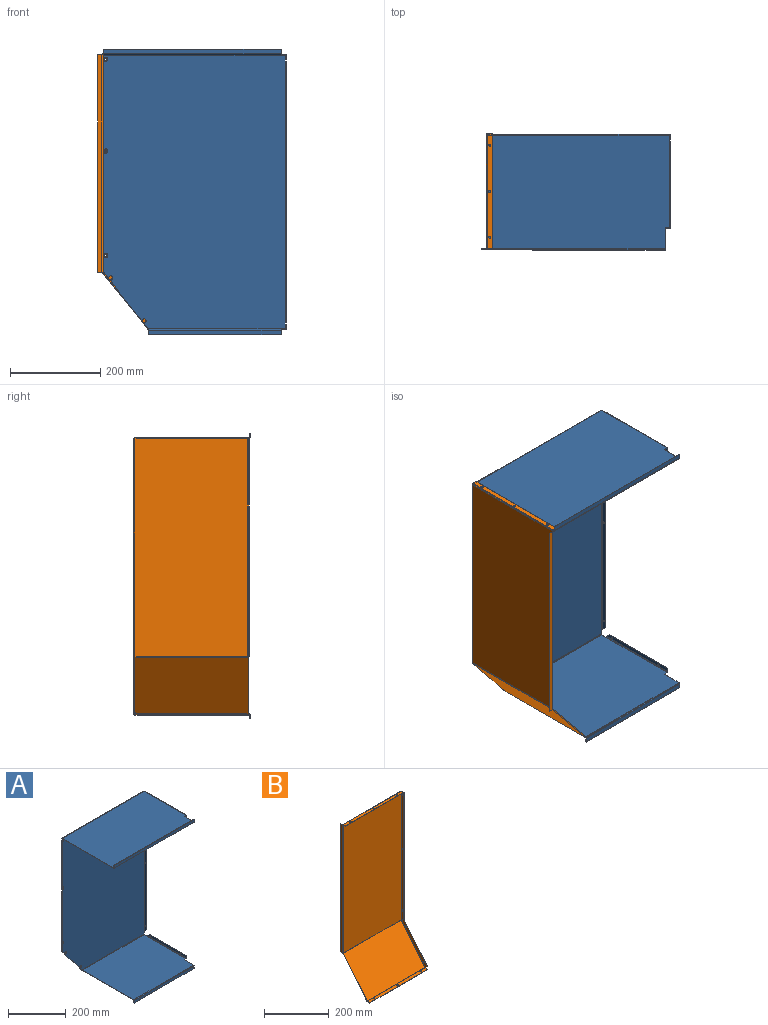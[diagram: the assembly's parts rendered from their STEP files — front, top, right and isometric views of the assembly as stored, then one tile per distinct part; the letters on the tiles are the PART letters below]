
ASSEMBLY  parts=2 mates=1
PART A: 86 faces, bbox 405.1x256.3x634.2 mm
  f0: plane 12.75x1.17mm, normal (1,0,0), area 14.9mm2, adj f14,f15,f25,f50
  f1: plane 7.57x1.17mm, normal (-1,0,0), area 8.8mm2, adj f13,f14,f15,f49
  f2: plane 12.75x1.17mm, normal (1,0,0), area 14.9mm2, adj f14,f15,f24,f29
  f3: plane 13.21x10.19mm, normal (-0.79,0,-0.61), area 19.5mm2, adj f4,f14,f15,f28
  f4: cylinder r=4.76mm len=9.53mm, axis (0,-1,0), area 31.2mm2, adj f3,f5,f14,f15
  f5: plane 92.97x71.75mm, normal (-0.79,0,-0.61), area 137.2mm2, adj f4,f6,f14,f15
  f6: cylinder r=4.76mm len=9.53mm, axis (0,-1,0), area 31.2mm2, adj f5,f7,f14,f15
  f7: plane 15.09x11.65mm, normal (-0.79,0,-0.61), area 22.3mm2, adj f6,f8,f14,f15
  f8: plane 34.52x1.17mm, normal (-1,0,0), area 40.3mm2, adj f7,f9,f14,f15
  f9: cylinder r=4.76mm len=9.53mm, axis (0,-1,0), area 31.2mm2, adj f8,f10,f14,f15
  f10: plane 228.63x1.17mm, normal (-1,0,0), area 267.1mm2, adj f9,f11,f14,f15
  f11: cylinder r=4.76mm len=9.53mm, axis (0,-1,0), area 31.2mm2, adj f10,f12,f14,f15
  f12: plane 200.06x1.17mm, normal (-1,0,0), area 233.7mm2, adj f11,f13,f14,f15
  f13: cylinder r=4.76mm len=9.53mm, axis (0,-1,0), area 31.2mm2, adj f1,f12,f14,f15
  f14: plane 606.45x402.79mm, normal (0,1,0), area 237770.7mm2, adj f0,f1,f2,f3,f4,f5,f6,f7
  f15: plane 606.45x402.79mm, normal (0,-1,0), area 237770.7mm2, adj f0,f1,f2,f3,f4,f5,f6,f7
  f16: plane 562.35x1.17mm, normal (0,-1,0), area 657.1mm2, adj f17,f21,f22,f23
  f17: plane 9.3x9.3mm, normal (0,-0.71,-0.71), area 15.4mm2, adj f16,f22,f23,f24
  f18: cylinder r=1.78mm len=3.56mm, axis (1,0,0), area 13.1mm2, adj f22,f23
  f19: cylinder r=1.78mm len=3.56mm, axis (1,0,0), area 13.1mm2, adj f22,f23
  f20: cylinder r=1.78mm len=3.56mm, axis (1,0,0), area 13.1mm2, adj f22,f23
  f21: plane 9.3x9.3mm, normal (0,-0.71,0.71), area 15.4mm2, adj f16,f22,f23,f25
  f22: plane 580.95x9.3mm, normal (1,0,0), area 5284.5mm2, adj f16,f17,f18,f19,f20,f21,f26
  f23: plane 580.95x9.3mm, normal (-1,0,0), area 5284.5mm2, adj f16,f17,f18,f19,f20,f21,f27
  f24: plane 2.34x2.34mm, normal (0,0,-1), area 3.2mm2, adj f2,f17,f26,f27
  f25: plane 2.34x2.34mm, normal (0,0,1), area 3.2mm2, adj f0,f21,f26,f27
  f26: cylinder r=2.34mm len=580.95mm, axis (0,0,-1), area 2132.4mm2, adj f14,f22,f24,f25
  f27: cylinder r=1.17mm len=580.95mm, axis (0,0,-1), area 1066.2mm2, adj f15,f23,f24,f25
  f28: bspline ~2.34x2.34mm, area 4mm2, adj f3,f30,f31,f33
  f29: plane 2.34x2.34mm, normal (1,0,0), area 3.2mm2, adj f2,f30,f31,f32
  f30: cylinder r=2.34mm len=305.36mm, axis (-1,0,0), area 1116.6mm2, adj f14,f28,f29,f36
  f31: cylinder r=1.17mm len=305.36mm, axis (-1,0,0), area 558.3mm2, adj f15,f28,f29,f37
  f32: plane 12.75x1.17mm, normal (1,0,0), area 14.9mm2, adj f29,f36,f37,f45
  f33: plane 251.66x1.17mm, normal (-1,0,0), area 294mm2, adj f28,f36,f37,f58
  f34: plane 8.99x1.17mm, normal (0,-1,0), area 10.5mm2, adj f35,f36,f37,f46
  f35: plane 46.94x1.17mm, normal (1,0,0), area 54.8mm2, adj f34,f36,f37,f59
  f36: plane 303.56x251.66mm, normal (0,0,-1), area 75971.7mm2, adj f30,f32,f33,f34,f35,f47,f61
  f37: plane 303.56x251.66mm, normal (0,0,1), area 75971.7mm2, adj f31,f32,f33,f34,f35,f48,f60
  f38: plane 182.68x1.17mm, normal (0,0,1), area 213.4mm2, adj f39,f42,f43,f44
  f39: plane 9.3x1.17mm, normal (0,-1,0), area 10.9mm2, adj f38,f43,f44,f46
  f40: cylinder r=1.78mm len=3.56mm, axis (1,0,0), area 13.1mm2, adj f43,f44
  f41: cylinder r=1.78mm len=3.56mm, axis (1,0,0), area 13.1mm2, adj f43,f44
  f42: plane 9.3x9.3mm, normal (0,0.71,0.71), area 15.4mm2, adj f38,f43,f44,f45
  f43: plane 191.97x9.3mm, normal (1,0,0), area 1721.6mm2, adj f38,f39,f40,f41,f42,f47
  f44: plane 191.97x9.3mm, normal (-1,0,0), area 1721.6mm2, adj f38,f39,f40,f41,f42,f48
  f45: plane 2.34x2.34mm, normal (0,1,0), area 3.2mm2, adj f32,f42,f47,f48
  f46: plane 2.34x2.34mm, normal (0,-1,0), area 3.2mm2, adj f34,f39,f47,f48
  f47: cylinder r=2.34mm len=191.97mm, axis (0,1,0), area 704.7mm2, adj f36,f43,f45,f46
  f48: cylinder r=1.17mm len=191.97mm, axis (0,1,0), area 352.3mm2, adj f37,f44,f45,f46
  f49: plane 2.34x2.34mm, normal (-1,0,0), area 3.2mm2, adj f1,f51,f52,f63
  f50: plane 2.34x2.34mm, normal (1,0,0), area 3.2mm2, adj f0,f51,f52,f62
  f51: cylinder r=2.34mm len=402.79mm, axis (-1,0,0), area 1478.5mm2, adj f14,f49,f50,f66
  f52: cylinder r=1.17mm len=402.79mm, axis (-1,0,0), area 739.3mm2, adj f15,f49,f50,f67
  f53: plane 294.56x1.17mm, normal (0,0,-1), area 344.2mm2, adj f54,f55,f56,f57
  f54: plane 10.36x1.17mm, normal (-1,0,0), area 12.1mm2, adj f53,f56,f57,f58
  f55: plane 10.36x1.17mm, normal (1,0,0), area 12.1mm2, adj f53,f56,f57,f59
  f56: plane 294.56x10.36mm, normal (0,1,0), area 3052.6mm2, adj f53,f54,f55,f61
  f57: plane 294.56x10.36mm, normal (0,-1,0), area 3052.6mm2, adj f53,f54,f55,f60
  f58: plane 2.34x2.34mm, normal (-1,0,0), area 3.2mm2, adj f33,f54,f60,f61
  f59: plane 2.34x2.34mm, normal (1,0,0), area 3.2mm2, adj f35,f55,f60,f61
  f60: cylinder r=2.34mm len=294.56mm, axis (-1,0,0), area 1081.2mm2, adj f37,f57,f58,f59
  f61: cylinder r=1.17mm len=294.56mm, axis (-1,0,0), area 540.6mm2, adj f36,f56,f58,f59
  f62: plane 12.75x1.17mm, normal (1,0,0), area 14.9mm2, adj f50,f66,f67,f73
  f63: plane 251.66x1.17mm, normal (-1,0,0), area 294mm2, adj f49,f66,f67,f82
  f64: plane 46.94x1.17mm, normal (1,0,0), area 54.8mm2, adj f65,f66,f67,f83
  f65: plane 8.99x1.17mm, normal (0,-1,0), area 10.5mm2, adj f64,f66,f67,f74
  f66: plane 402.79x251.66mm, normal (0,0,1), area 100946.2mm2, adj f51,f62,f63,f64,f65,f75,f85
  f67: plane 402.79x251.66mm, normal (0,0,-1), area 100946.2mm2, adj f52,f62,f63,f64,f65,f76,f84
  f68: plane 182.68x1.17mm, normal (0,0,-1), area 213.4mm2, adj f69,f70,f71,f72
  f69: plane 9.3x9.3mm, normal (0,0.71,-0.71), area 15.4mm2, adj f68,f71,f72,f73
  f70: plane 9.3x1.17mm, normal (0,-1,0), area 10.9mm2, adj f68,f71,f72,f74
  f71: plane 191.97x9.3mm, normal (1,0,0), area 1741.4mm2, adj f68,f69,f70,f75
  f72: plane 191.97x9.3mm, normal (-1,0,0), area 1741.4mm2, adj f68,f69,f70,f76
  f73: plane 2.34x2.34mm, normal (0,1,0), area 3.2mm2, adj f62,f69,f75,f76
  f74: plane 2.34x2.34mm, normal (0,-1,0), area 3.2mm2, adj f65,f70,f75,f76
  f75: cylinder r=2.34mm len=191.97mm, axis (0,1,0), area 704.7mm2, adj f66,f71,f73,f74
  f76: cylinder r=1.17mm len=191.97mm, axis (0,1,0), area 352.3mm2, adj f67,f72,f73,f74
  f77: plane 10.36x1.17mm, normal (-1,0,0), area 12.1mm2, adj f78,f80,f81,f82
  f78: plane 393.8x1.17mm, normal (0,0,1), area 460.1mm2, adj f77,f79,f80,f81
  f79: plane 10.36x1.17mm, normal (1,0,0), area 12.1mm2, adj f78,f80,f81,f83
  f80: plane 393.8x10.36mm, normal (0,1,0), area 4081mm2, adj f77,f78,f79,f85
  f81: plane 393.8x10.36mm, normal (0,-1,0), area 4081mm2, adj f77,f78,f79,f84
  f82: plane 2.34x2.34mm, normal (-1,0,0), area 3.2mm2, adj f63,f77,f84,f85
  f83: plane 2.34x2.34mm, normal (1,0,0), area 3.2mm2, adj f64,f79,f84,f85
  f84: cylinder r=2.34mm len=393.8mm, axis (-1,0,0), area 1445.5mm2, adj f67,f81,f82,f83
  f85: cylinder r=1.17mm len=393.8mm, axis (-1,0,0), area 722.8mm2, adj f66,f80,f82,f83
PART B: 71 faces, bbox 255.2x127.5x615.8 mm
  f0: plane 1.17x0.62mm, normal (1,0,0), area 0.7mm2, adj f1,f2,f12,f25
  f1: plane 483.3x250.5mm, normal (0,1,0), area 121065.1mm2, adj f0,f13,f23,f26,f40
  f2: plane 483.3x250.5mm, normal (0,-1,0), area 121065.1mm2, adj f0,f14,f22,f27,f41
  f3: plane 479.01x1.17mm, normal (0,-1,0), area 559.7mm2, adj f4,f8,f9,f10
  f4: plane 10.36x3.67mm, normal (0,-0.33,-0.94), area 12.8mm2, adj f3,f9,f10,f12
  f5: cylinder r=2.39mm len=4.78mm, axis (1,0,0), area 17.5mm2, adj f9,f10
  f6: cylinder r=2.39mm len=4.78mm, axis (1,0,0), area 17.5mm2, adj f9,f10
  f7: cylinder r=2.39mm len=4.78mm, axis (1,0,0), area 17.5mm2, adj f9,f10
  f8: plane 10.36x1.17mm, normal (0,0,1), area 12.1mm2, adj f3,f9,f10,f11
  f9: plane 482.68x10.36mm, normal (1,0,0), area 4929.4mm2, adj f3,f4,f5,f6,f7,f8,f13
  f10: plane 482.68x10.36mm, normal (-1,0,0), area 4929.4mm2, adj f3,f4,f5,f6,f7,f8,f14
  f11: plane 2.34x2.34mm, normal (0,0,1), area 3.2mm2, adj f8,f13,f14,f39
  f12: plane 2.34x2.34mm, normal (0,0,-1), area 3.2mm2, adj f0,f4,f13,f14
  f13: cylinder r=2.34mm len=482.68mm, axis (0,0,1), area 1771.8mm2, adj f1,f9,f11,f12
  f14: cylinder r=1.17mm len=482.68mm, axis (0,0,1), area 885.9mm2, adj f2,f10,f11,f12
  f15: plane 483.3x1.17mm, normal (0,1,0), area 564.7mm2, adj f16,f17,f18,f19
  f16: plane 9.27x1.17mm, normal (0,0,1), area 10.8mm2, adj f15,f18,f19,f20
  f17: plane 9.27x1.17mm, normal (0,0,-1), area 10.8mm2, adj f15,f18,f19,f21
  f18: plane 483.3x9.27mm, normal (1,0,0), area 4480.7mm2, adj f15,f16,f17,f23
  f19: plane 483.3x9.27mm, normal (-1,0,0), area 4480.7mm2, adj f15,f16,f17,f22
  f20: plane 2.34x2.34mm, normal (0,0,1), area 3.2mm2, adj f16,f22,f23,f38
  f21: plane 2.34x2.34mm, normal (0,0,-1), area 3.2mm2, adj f17,f22,f23,f24
  f22: cylinder r=2.34mm len=483.3mm, axis (0,0,1), area 1774mm2, adj f2,f19,f20,f21
  f23: cylinder r=1.17mm len=483.3mm, axis (0,0,1), area 887mm2, adj f1,f18,f20,f21
  f24: plane 1.47x1.43mm, normal (-1,0,0), area 1.4mm2, adj f21,f26,f27,f42
  f25: plane 1.47x1.43mm, normal (1,0,0), area 1.4mm2, adj f0,f26,f27,f43
  f26: cylinder r=2.34mm len=250.5mm, axis (-1,0,0), area 398.4mm2, adj f1,f24,f25,f45
  f27: cylinder r=1.17mm len=250.5mm, axis (-1,0,0), area 199.2mm2, adj f2,f24,f25,f46
  f28: plane 1.17x1.17mm, normal (0,1,0), area 1.4mm2, adj f29,f36,f37,f39
  f29: plane 10.36x1.17mm, normal (1,0,0), area 12.1mm2, adj f28,f35,f36,f37
  f30: plane 1.17x1.17mm, normal (0,1,0), area 1.4mm2, adj f31,f36,f37,f38
  f31: plane 10.36x1.17mm, normal (-1,0,0), area 12.1mm2, adj f30,f35,f36,f37
  f32: cylinder r=2.39mm len=4.78mm, axis (0,0,1), area 17.5mm2, adj f36,f37
  f33: cylinder r=2.39mm len=4.78mm, axis (0,0,1), area 17.5mm2, adj f36,f37
  f34: cylinder r=2.39mm len=4.78mm, axis (0,0,1), area 17.5mm2, adj f36,f37
  f35: plane 252.83x1.17mm, normal (0,-1,0), area 295.4mm2, adj f29,f31,f36,f37
  f36: plane 252.83x10.36mm, normal (0,0,1), area 2566.4mm2, adj f28,f29,f30,f31,f32,f33,f34,f35
  f37: plane 252.83x10.36mm, normal (0,0,-1), area 2566.4mm2, adj f28,f29,f30,f31,f32,f33,f34,f35
  f38: plane 2.34x2.34mm, normal (-1,0,0), area 3.2mm2, adj f20,f30,f40,f41
  f39: plane 2.34x2.34mm, normal (1,0,0), area 3.2mm2, adj f11,f28,f40,f41
  f40: cylinder r=2.34mm len=250.5mm, axis (-1,0,0), area 919.5mm2, adj f1,f36,f38,f39
  f41: cylinder r=1.17mm len=250.5mm, axis (-1,0,0), area 459.7mm2, adj f2,f37,f38,f39
  f42: plane 1.17x0.91mm, normal (0,0.63,0.78), area 1.4mm2, adj f24,f44,f45,f46
  f43: plane 1.3x1.22mm, normal (1,0,0), area 0.7mm2, adj f25,f45,f46,f56
  f44: plane 128.58x104.44mm, normal (-1,0,0), area 192.2mm2, adj f42,f45,f46,f67
  f45: plane 251.66x127.85mm, normal (0,0.78,-0.63), area 41400.2mm2, adj f26,f42,f43,f44,f57,f69
  f46: plane 251.66x127.85mm, normal (0,-0.78,0.63), area 41400.2mm2, adj f27,f42,f43,f44,f58,f70
  f47: plane 1.17x0.43mm, normal (0,0.78,-0.63), area 0.7mm2, adj f49,f53,f54,f55
  f48: plane 124.95x101.18mm, normal (0,-0.78,0.63), area 187.8mm2, adj f49,f52,f53,f54
  f49: plane 8.05x6.52mm, normal (0,-0.63,-0.78), area 12.1mm2, adj f47,f48,f53,f54
  f50: cylinder r=2.39mm len=4.78mm, axis (1,0,0), area 17.5mm2, adj f53,f54
  f51: cylinder r=2.39mm len=4.78mm, axis (1,0,0), area 17.5mm2, adj f53,f54
  f52: plane 10.36x3.67mm, normal (0,0.33,0.94), area 12.8mm2, adj f48,f53,f54,f56
  f53: plane 131.47x111.54mm, normal (1,0,0), area 1649.3mm2, adj f47,f48,f49,f50,f51,f52,f57
  f54: plane 131.47x111.54mm, normal (-1,0,0), area 1649.3mm2, adj f47,f48,f49,f50,f51,f52,f58
  f55: plane 2.34x1.82mm, normal (0,-0.63,-0.78), area 3.2mm2, adj f47,f57,f58,f68
  f56: plane 2.34x1.82mm, normal (0,0.63,0.78), area 3.2mm2, adj f43,f52,f57,f58
  f57: cylinder r=2.34mm len=128.83mm, axis (0,-0.63,-0.78), area 601.6mm2, adj f45,f53,f55,f56
  f58: cylinder r=1.17mm len=128.1mm, axis (0,-0.63,-0.78), area 300.8mm2, adj f46,f54,f55,f56
  f59: plane 251.66x1.17mm, normal (0,-1,0), area 294mm2, adj f60,f64,f65,f66
  f60: plane 11.15x1.17mm, normal (-1,0,0), area 13mm2, adj f59,f65,f66,f67
  f61: cylinder r=2.39mm len=4.78mm, axis (0,0,-1), area 17.5mm2, adj f65,f66
  f62: cylinder r=2.39mm len=4.78mm, axis (0,0,-1), area 17.5mm2, adj f65,f66
  f63: cylinder r=2.39mm len=4.78mm, axis (0,0,-1), area 17.5mm2, adj f65,f66
  f64: plane 11.15x1.17mm, normal (1,0,0), area 13mm2, adj f59,f65,f66,f68
  f65: plane 251.66x11.15mm, normal (0,0,-1), area 2753.2mm2, adj f59,f60,f61,f62,f63,f64,f69
  f66: plane 251.66x11.15mm, normal (0,0,1), area 2753.2mm2, adj f59,f60,f61,f62,f63,f64,f70
  f67: plane 1.82x1.6mm, normal (-1,0,0), area 1.8mm2, adj f44,f60,f69,f70
  f68: plane 1.82x1.6mm, normal (1,0,0), area 1.8mm2, adj f55,f64,f69,f70
  f69: cylinder r=2.34mm len=251.66mm, axis (-1,0,0), area 523.5mm2, adj f45,f65,f67,f68
  f70: cylinder r=1.17mm len=251.66mm, axis (-1,0,0), area 261.7mm2, adj f46,f66,f67,f68
PLACE A at identity fixed
PLACE B rot(axis=(0,0,1),90deg) t=(-203.17,1.75,-179.27)mm
MATE fastened B.f7 <-> A.f13  axis (0,-1,0) through (-197.49,128.17,294.08)mm
